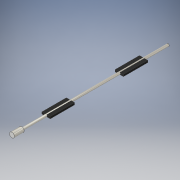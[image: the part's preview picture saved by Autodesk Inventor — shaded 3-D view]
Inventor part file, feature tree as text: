
AUTODESK INVENTOR PART (.ipt)
format: ipt  version: 2018 (Build 220112000, 112)  size: 138,240 bytes
history: native  units: in
note: dims shown in document units (in); Inventor stores cm internally (conversion verified against a paired STEP export)
features: extrude x3, sketch x3, mirror x1
ambient origin geometry x8: Origin, YZ Plane, XZ Plane, XY Plane, X Axis, Y Axis, Z Axis, Center Point
bodies: Solid1 (feature_tree)
feature tree (7):
  extrude  "Extrusion1"  Depth=11.811in TaperAngle=0.0deg
  extrude  "Extrusion2"  Depth=1.9685in
  mirror  "Mirror1"
  extrude  "Extrusion3"  Depth=1.9685in
  sketch  "Sketch1"  dims[d0=0.1969in d1=11.811in d2=0.0in]
  sketch  "Sketch2"  dims[d3=0.2756in d4=1.9685in]
  sketch  "Sketch3"  dims[d5=0.2756in d6=1.9685in d7=0.0in d8=5.9055in d9=0.3346in d10=1.9685in d11=0.1575in d12=0.0in d13=0.3937in d14=0.7874in d15=0.0in]
